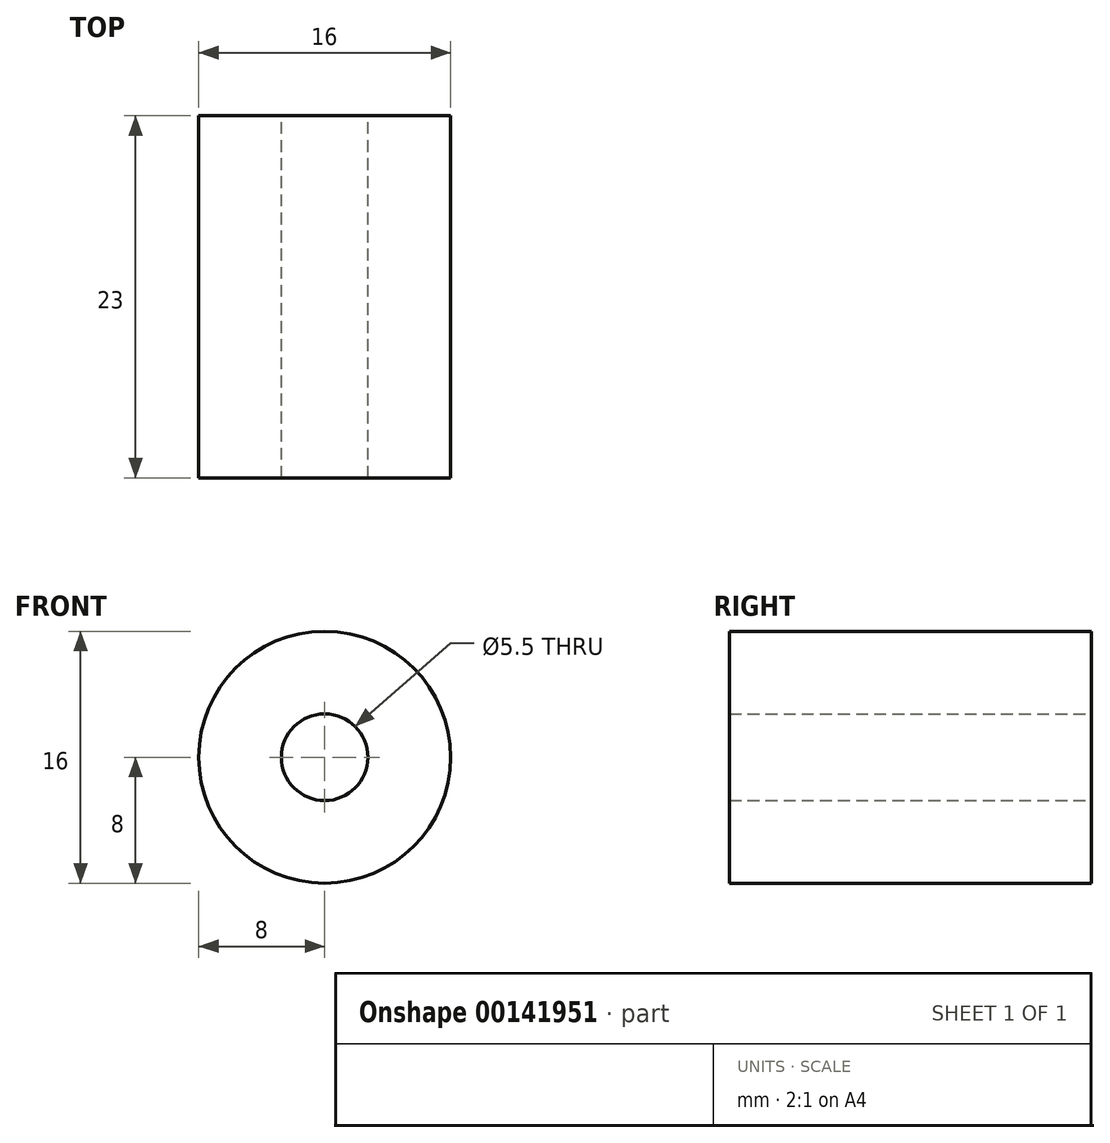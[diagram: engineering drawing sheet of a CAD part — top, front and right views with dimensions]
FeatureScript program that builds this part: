
annotation { "Feature Type Name" : "Feature", "Feature Type Description" : "" }
export const myFeature = defineFeature(function(context is Context, id is Id, definition is map)
    precondition{}
    {
        {
            var Q0;
            Q0=qCreatedBy(makeId("Front.planeOp"),FACE);
            var sketch = newSketch(context, id + "F0", { "sketchPlane" : qUnion([Q0])});
            skCircle(sketch, "E0", {"center": v(0, 0) * mm, "radius": 2.75 * mm});
            skCircle(sketch, "E1", {"center": v(0, 0) * mm, "radius": 8 * mm});
            skSolve(sketch);
        }
        {
            var Q0;
            Q0=makeQuery(id+"F0.imprint","IMPRINT",FACE,{"disambiguationData":[TD([[makeQuery(id+"F0.imprint","IMPRINT",EDGE,{"derivedFrom":sQuery(id+"F0.wireOp",EDGE,"E0")}),-1.0]])]});
            extrude(context, id + "F1", {"entities" : qUnion([Q0]), "depth" : 23 * mm, "offsetDistance" : 25 * mm});
        }
    });
